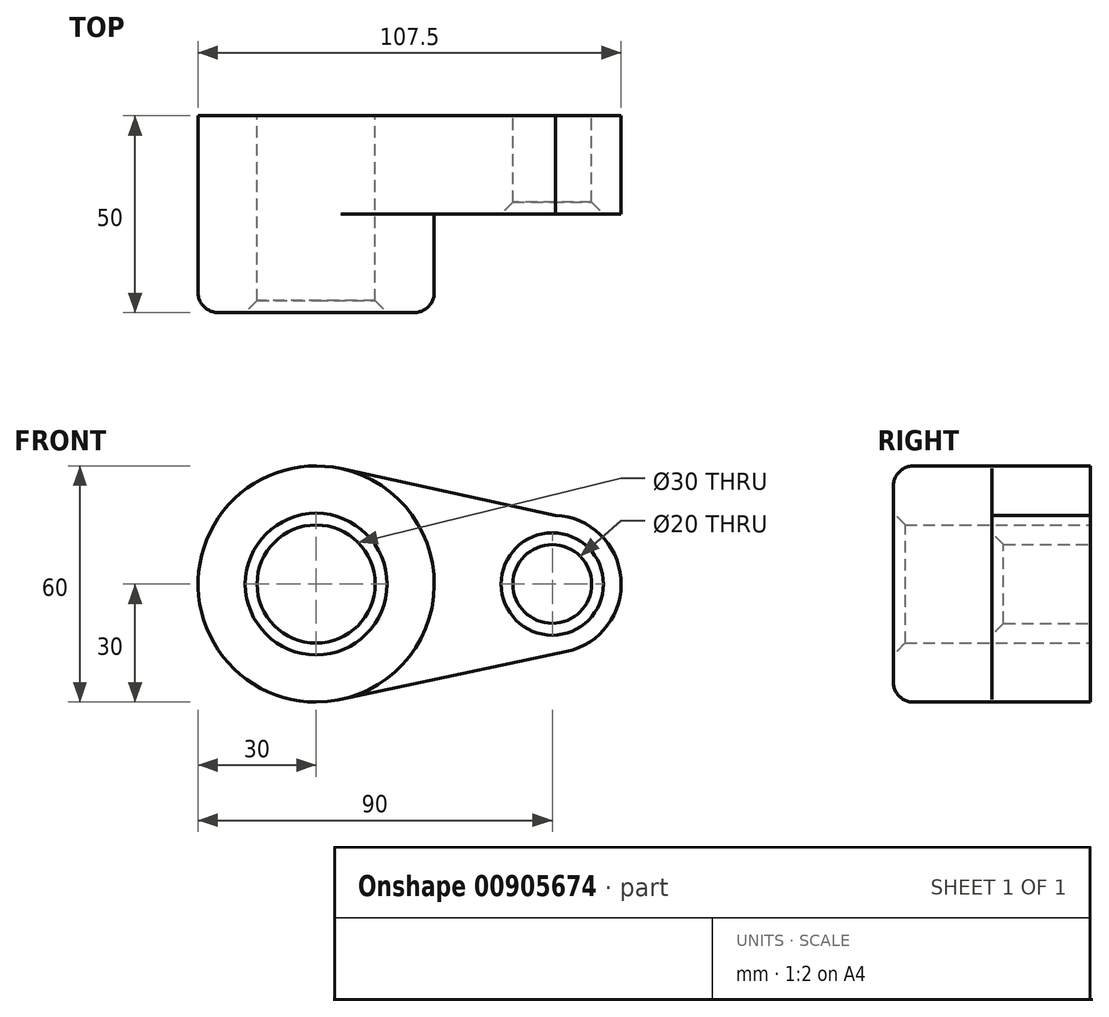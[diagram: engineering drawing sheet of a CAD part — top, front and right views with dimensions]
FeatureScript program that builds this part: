
annotation { "Feature Type Name" : "Feature", "Feature Type Description" : "" }
export const myFeature = defineFeature(function(context is Context, id is Id, definition is map)
    precondition{}
    {
        {
            var Q0;
            Q0=qCreatedBy(makeId("Front.planeOp"),FACE);
            var sketch = newSketch(context, id + "F0", { "sketchPlane" : qUnion([Q0])});
            skCircle(sketch, "E0", {"center": v(0, 0) * mm, "radius": 30 * mm});
            skCircle(sketch, "E1", {"center": v(60, 0) * mm, "radius": 17.5 * mm});
            skLineSegment(sketch, "E2", {"start": v(6.37, 29.32) * mm, "end": v(60.8, 17.48) * mm});
            skLineSegment(sketch, "E3", {"start": v(6.25, -29.34) * mm, "end": v(63.65, -17.12) * mm});
            skCircle(sketch, "E4", {"center": v(0, 0) * mm, "radius": 15 * mm});
            skCircle(sketch, "E5", {"center": v(60, 0) * mm, "radius": 10 * mm});
            skSolve(sketch);
        }
        {
            var Q0;
            Q0=makeQuery(id+"F0.imprint","IMPRINT",FACE,{"disambiguationData":[TD([[makeQuery(id+"F0.imprint","IMPRINT",EDGE,{"derivedFrom":sQuery(id+"F0.wireOp",EDGE,"E4")}),-1.0]])]});
            var Q1;
            {var subQ0=sQuery(id+"F0.wireOp",EDGE,"E2");Q1=makeQuery(id+"F0.imprint","IMPRINT",FACE,{"disambiguationData":[TD([[makeQuery(id+"F0.imprint","IMPRINT",EDGE,{"derivedFrom":subQ0}),-1.0]])]});}
            var Q2;
            Q2=makeQuery(id+"F0.imprint","IMPRINT",FACE,{"disambiguationData":[TD([[makeQuery(id+"F0.imprint","IMPRINT",EDGE,{"derivedFrom":sQuery(id+"F0.wireOp",EDGE,"E5")}),-1.0]])]});
            extrude(context, id + "F1", {"entities" : qUnion([Q0, Q1, Q2]), "depth" : 25 * mm, "offsetDistance" : 25.4 * mm});
        }
        {
            var Q0;
            Q0=makeQuery(id+"F0.imprint","IMPRINT",FACE,{"disambiguationData":[TD([[makeQuery(id+"F0.imprint","IMPRINT",EDGE,{"derivedFrom":sQuery(id+"F0.wireOp",EDGE,"E4")}),-1.0]])]});
            extrude(context, id + "F2", {"entities" : qUnion([Q0]), "operationType" : NewBodyOperationType.ADD, "depth" : 50 * mm, "offsetDistance" : 25.4 * mm});
        }
        {
            var Q0;
            Q0=makeQuery(id+"F2.opExtrude","CAP_EDGE",EDGE,{"disambiguationData":[OSD([sQuery(id+"F0.wireOp",EDGE,"E0")])],"isStart":false});
            fillet(context, id + "F3", {"entities" : qUnion([Q0]), "radius" : 5.08 * mm, "tangentPropagation" : true, "allowEdgeOverflow" : false});
        }
        {
            var Q0;
            Q0=makeQuery(id+"F2.opExtrude","CAP_EDGE",EDGE,{"disambiguationData":[OSD([sQuery(id+"F0.wireOp",EDGE,"E4")])],"isStart":false});
            var Q1;
            Q1=makeQuery(id+"F1.opExtrude","CAP_EDGE",EDGE,{"disambiguationData":[OSD([sQuery(id+"F0.wireOp",EDGE,"E5")])],"isStart":false});
            chamfer(context, id + "F4", {"entities" : qUnion([Q0, Q1]), "width" : 3 * mm, "tangentPropagation" : true});
        }
    });
